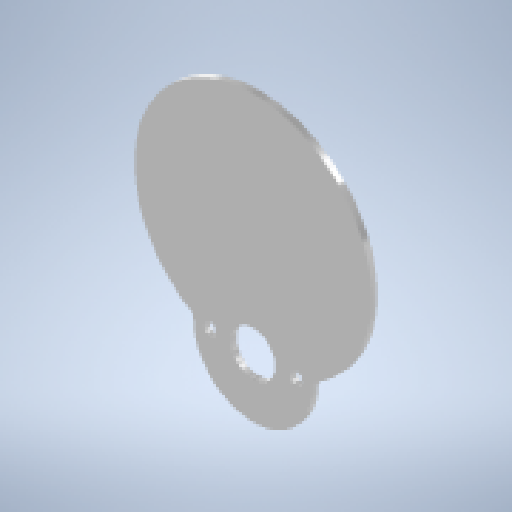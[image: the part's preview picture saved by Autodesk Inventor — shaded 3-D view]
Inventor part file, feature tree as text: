
AUTODESK INVENTOR PART (.ipt)
format: ipt  version: 2024 (Build 280153000, 153)  size: 322,560 bytes
history: native  units: mm
features: sketch x8, extrude x4, hole x4, projected_geometry x2, other x1, pattern_circular x1, fillet x1
ambient origin geometry x8: Origin, YZ Plane, XZ Plane, XY Plane, X Axis, Y Axis, Z Axis, Center Point
bodies: Body1 (feature_tree)
feature tree (21):
  other  "ソリッド1"
  extrude  "押し出し1"  Depth=80.0mm
  hole  "穴1"  [1 undecoded]
  hole  "穴2"  [1 undecoded]
  hole  "穴3"  [1 undecoded]
  extrude  "押し出し2"  Depth=14.5mm
  pattern_circular  "円形状パターン1"  [2 undecoded]
  fillet  "フィレット1"  Radius=10.0mm
  extrude  "押し出し3"  Depth=2.0mm TaperAngle=0.0deg
  hole  "穴4"  [1 undecoded]
  extrude  "押し出し4"  Depth=5.0mm
  sketch  "スケッチ1"
  sketch  "スケッチ2"
  sketch  "スケッチ3"
  projected_geometry  "投影ループ1"
  sketch  "スケッチ4"
  sketch  "スケッチ5"
  sketch  "スケッチ6"
  projected_geometry  "投影ループ2"
  sketch  "スケッチ7"
  sketch  "スケッチ8"
note: 6 required parameter values undecoded (feature->parameter linkage not recoverable at this tier; creation-order binding heuristic only, values carry confidence <= 0.55)
